# Revit family: 3-563-xxx Siren Wall Sconce
name_source: partatom
category: Lighting Fixtures
revit_build: Autodesk Revit 2018 (Build: 20170223_1515(x64)
units: mm (PartAtom-declared; Revit-internal decimal feet)

## family parameters
Always vertical = Yes
Cut with Voids When Loaded = No
Host = Wall
Light Source = Yes
OmniClass Number = 23.80.70.00
OmniClass Title = Lighting
Part Type = Normal
Room Calculation Point = No
Round Connector Dimension = Use Diameter
Shared = No

## types (4) — shared parameters
Color Filter = 16777215
Dimming Lamp Color Temperature Shift = <None>
Lamp = LED Array
Light Source Symbol Size = 24 "
Manufacturer = Oxygen Lighting and Fans
Model = 3-563-xxx / Siren Wall Sconce
References = Ref. 3 = 120 V / Ref. 37 = 277 V
URL = www.oxygenlighting.com
Voltage = 120 V
Voltage Input = 120 V or 277 V - 50/60 Hz
Wattage Comments = 1 x 10.1 W at 120 V

## per-type parameters (varying)
| type | Main Diffuser | Metal Finish |
| 3-563-114 / Polished Chrome - White Opal Glass | White Opal Glass | 14 - Polished Chrome |
| 3-563-224 / Satin Nickel - Matte White Acrylic | Matte White Acrylic | 24 - Satin Nickel |
| 3-563-124 / Satin Nickel - White Opal Glass | White Opal Glass | 24 - Satin Nickel |
| 3-563-214 / Polished Chrome - Matte White Acrylic | Matte White Acrylic | 14 - Polished Chrome |

## geometry (parser evidence)
native form markers: Sweep x5
no freeform markers — native parametric forms only
